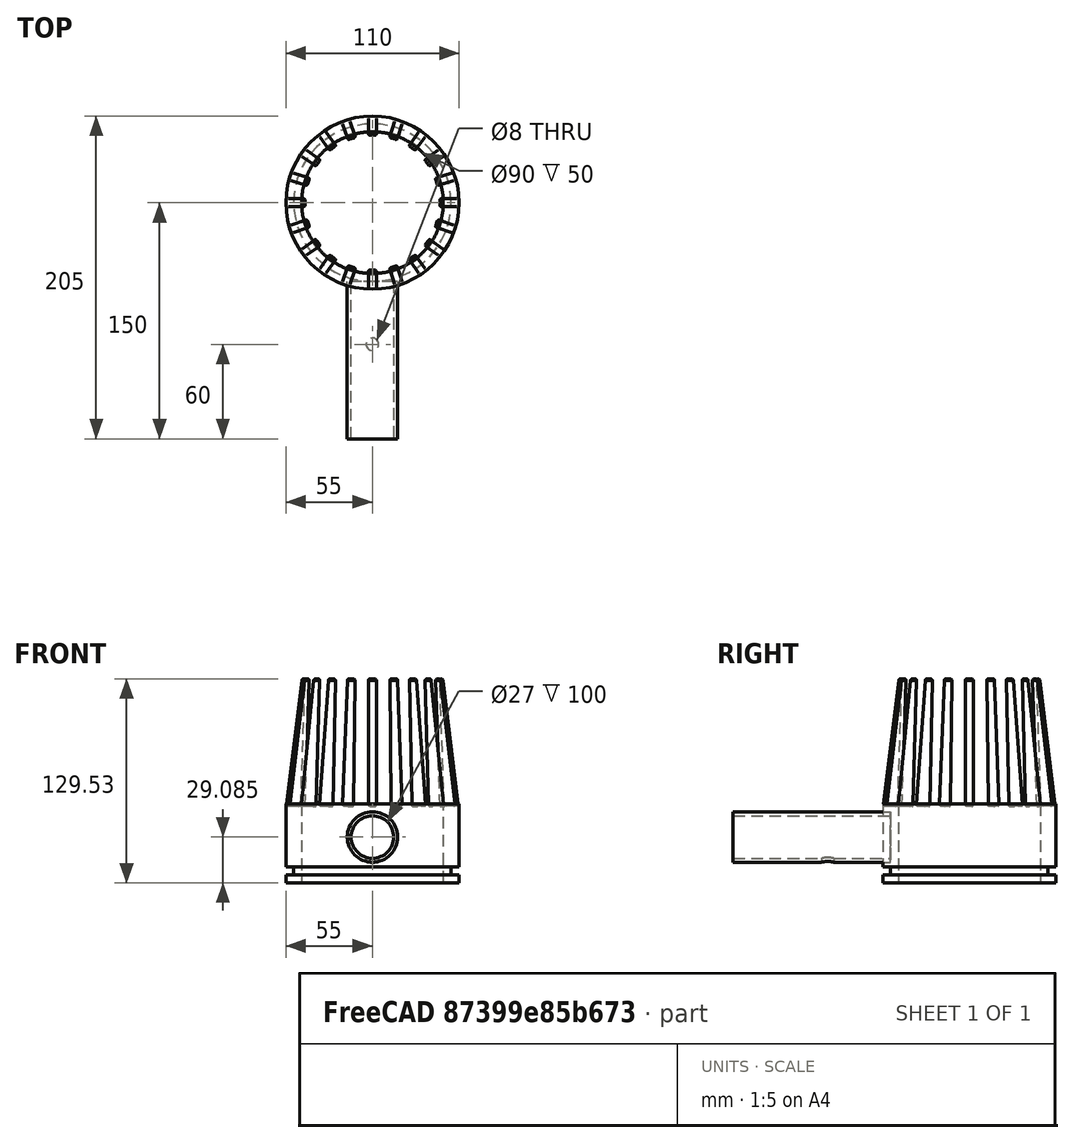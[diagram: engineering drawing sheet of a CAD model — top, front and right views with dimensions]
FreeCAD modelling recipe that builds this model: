
FCSTD DOCUMENT  (FreeCAD 1.1RUnknown)
Label: Picker
License: All rights reserved
LicenseURL: https://en.wikipedia.org/wiki/All_rights_reserved
objects: Part::Fillet×20, Sketcher::SketchObject×5, Part::Face×5, Part::Extrusion×5, Part::Cut×2, Part::Compound×2, Part::Plane×1
note: 45 computed .brp shape members not serialized (recipe doc carries the construction recipe); baked Part::Feature solids carry a one-line shape summary decoded from their .brp

FEATURE [Sketcher::SketchObject] Sketch
  ArcFitTolerance = 1e-06
  ExternalTypes = [0]
  FullyConstrained = true
  MakeInternals = false
  _ExternalGeoVersion = 1
  sketch-geometry (2):
    g0: Circle CenterX=0 CenterY=0 CenterZ=0 NormalX=0 NormalY=0 NormalZ=1 AngleXU=0 Radius=45
    g1: Circle CenterX=0 CenterY=0 CenterZ=0 NormalX=0 NormalY=0 NormalZ=1 AngleXU=0 Radius=55
  constraints (4):
    c: Diameter(g0) = 90
    c: Coincident(g0,g-1)
    c: Diameter(g1) = 110
    c: Coincident(g1,g0)
FEATURE [Part::Face] Face
  FaceMakerClass = Part::FaceMakerBullseye
  Sources = -> [Sketch]
FEATURE [Part::Extrusion] Extrude
  Base = -> Sketch
  Dir = (0,0,1)
  DirMode = 2
  FaceMakerClass = Part::FaceMakerBullseye
  FaceMakerMode = 3
  InnerWireTaper = 0
  LengthFwd = 40
  LengthRev = 10
  Solid = true
  Symmetric = false
FEATURE [Sketcher::SketchObject] Sketch001
  ArcFitTolerance = 1e-06
  AttachmentSupport = -> [Face]
  ExternalTypes = [0]
  FullyConstrained = true
  MakeInternals = false
  MapMode = 2
  _ExternalGeoVersion = 1
  sketch-geometry (2):
    g0: Circle CenterX=0 CenterY=0 CenterZ=0 NormalX=0 NormalY=0 NormalZ=1 AngleXU=0 Radius=55
    g1: Circle CenterX=0 CenterY=0 CenterZ=0 NormalX=0 NormalY=0 NormalZ=1 AngleXU=0 Radius=50
  constraints (4):
    c: Diameter(g0) = 110
    c: Coincident(g0,g-1)
    c: Diameter(g1) = 100
    c: Coincident(g1,g0)
FEATURE [Part::Face] Face001
  FaceMakerClass = Part::FaceMakerBullseye
  Sources = -> [Sketch001]
FEATURE [Part::Extrusion] Extrude001
  Base = -> Face001
  Dir = (0,0,1)
  DirMode = 2
  FaceMakerClass = Part::FaceMakerBullseye
  FaceMakerMode = 3
  InnerWireTaper = 0
  LengthFwd = 0
  LengthRev = 5
  Solid = false
  Symmetric = false
FEATURE [Part::Cut] Cut
  Base = -> Extrude
  Refine = true
  Tool = -> Extrude001
FEATURE [Sketcher::SketchObject] Sketch002
  ArcFitTolerance = 1e-06
  ExternalTypes = [0]
  FullyConstrained = true
  MakeInternals = false
  Placement = pos=(0,0,0) rot=(1,0,0;1.5708rad)
  _ExternalGeoVersion = 1
  sketch-geometry (6):
    g0: LineSegment StartX=-54 StartY=40 StartZ=0 EndX=-45 EndY=40 EndZ=0
    g1: LineSegment StartX=-45 StartY=40 StartZ=0 EndX=-45 EndY=120 EndZ=0
    g2: ArcOfCircle CenterX=-46 CenterY=120 CenterZ=0 NormalX=0 NormalY=0 NormalZ=1 AngleXU=0 Radius=1 StartAngle=-1.8e-15 EndAngle=1.5708
    g3: LineSegment StartX=-54 StartY=40 StartZ=0 EndX=-47 EndY=120 EndZ=0
    g4: ArcOfCircle CenterX=-46 CenterY=120 CenterZ=0 NormalX=0 NormalY=0 NormalZ=1 AngleXU=0 Radius=1 StartAngle=1.5708 EndAngle=3.14159
    g5: LineSegment [constr] StartX=-54 StartY=40 StartZ=0 EndX=0 EndY=40 EndZ=0
  constraints (19):
    c: Horizontal(g0)
    c: Distance(g1) = 80
    c: Vertical(g1)
    c: Coincident(g1,g0)
    c: Angle(g2) = 1.5708
    c: Coincident(g2,g1)
    c: Horizontal(g2,g1)
    c: Radius(g2) = 1
    c: Coincident(g3,g0)
    c: Coincident(g4,g2)
    c: Coincident(g4,g2)
    c: Coincident(g4,g3)
    c: Horizontal(g3,g2)
    c: Coincident(g5,g0)
    c: PointOnObject(g5,g-2)
    c: Horizontal(g5)
    c: Distance(g5,g-1) = 40
    c: DistanceX(g-2,g0) = -45
    c: Distance(g0) = 9
FEATURE [Part::Face] Face002
  FaceMakerClass = Part::FaceMakerBullseye
  Sources = -> [Sketch002]
FEATURE [Part::Extrusion] Extrude002
  Base = -> Sketch002
  Dir = (0,-1,2e-16)
  DirMode = 2
  FaceMakerClass = Part::FaceMakerBullseye
  FaceMakerMode = 3
  InnerWireTaper = 0
  LengthFwd = 5
  LengthRev = 5
  Placement = pos=(-2,0,0) rot=(0,1,0;0.034907rad)
  Solid = true
  Symmetric = true
FEATURE [Part::Fillet] Fillet  label="Bristle"
  Base = -> Extrude002
  EdgeLinks = -> Extrude002 [Edge3,Edge4,Edge6,Edge7,Edge9,Edge10,Edge12,Edge13,Edge14,Edge15]
  Edges = 10 edges r=1: [Edge3,Edge4,Edge6,Edge7,Edge9,Edge10,Edge12,Edge13,Edge14,Edge15]
FEATURE [Part::Fillet] Fillet001  label="Bristle001"
  Base = -> Extrude002
  EdgeLinks = -> Extrude002 [Edge3,Edge4,Edge6,Edge7,Edge9,Edge10,Edge12,Edge13,Edge14,Edge15]
  Edges = 10 edges r=1: [Edge3,Edge4,Edge6,Edge7,Edge9,Edge10,Edge12,Edge13,Edge14,Edge15]
  Placement = pos=(0,0,0) rot=(0,0,1;0.314159rad)
FEATURE [Part::Fillet] Fillet002  label="Bristle002"
  Base = -> Extrude002
  EdgeLinks = -> Extrude002 [Edge3,Edge4,Edge6,Edge7,Edge9,Edge10,Edge12,Edge13,Edge14,Edge15]
  Edges = 10 edges r=1: [Edge3,Edge4,Edge6,Edge7,Edge9,Edge10,Edge12,Edge13,Edge14,Edge15]
  Placement = pos=(0,0,0) rot=(0,0,1;0.628319rad)
FEATURE [Part::Fillet] Fillet003  label="Bristle003"
  Base = -> Extrude002
  EdgeLinks = -> Extrude002 [Edge3,Edge4,Edge6,Edge7,Edge9,Edge10,Edge12,Edge13,Edge14,Edge15]
  Edges = 10 edges r=1: [Edge3,Edge4,Edge6,Edge7,Edge9,Edge10,Edge12,Edge13,Edge14,Edge15]
  Placement = pos=(0,0,0) rot=(0,0,1;0.942478rad)
FEATURE [Part::Fillet] Fillet004  label="Bristle004"
  Base = -> Extrude002
  EdgeLinks = -> Extrude002 [Edge3,Edge4,Edge6,Edge7,Edge9,Edge10,Edge12,Edge13,Edge14,Edge15]
  Edges = 10 edges r=1: [Edge3,Edge4,Edge6,Edge7,Edge9,Edge10,Edge12,Edge13,Edge14,Edge15]
  Placement = pos=(0,0,0) rot=(0,0,1;1.25664rad)
FEATURE [Part::Fillet] Fillet005  label="Bristle005"
  Base = -> Extrude002
  EdgeLinks = -> Extrude002 [Edge3,Edge4,Edge6,Edge7,Edge9,Edge10,Edge12,Edge13,Edge14,Edge15]
  Edges = 10 edges r=1: [Edge3,Edge4,Edge6,Edge7,Edge9,Edge10,Edge12,Edge13,Edge14,Edge15]
  Placement = pos=(0,0,0) rot=(0,0,1;1.5708rad)
FEATURE [Part::Fillet] Fillet006  label="Bristle006"
  Base = -> Extrude002
  EdgeLinks = -> Extrude002 [Edge3,Edge4,Edge6,Edge7,Edge9,Edge10,Edge12,Edge13,Edge14,Edge15]
  Edges = 10 edges r=1: [Edge3,Edge4,Edge6,Edge7,Edge9,Edge10,Edge12,Edge13,Edge14,Edge15]
  Placement = pos=(0,0,0) rot=(0,0,1;1.88496rad)
FEATURE [Part::Fillet] Fillet007  label="Bristle007"
  Base = -> Extrude002
  EdgeLinks = -> Extrude002 [Edge3,Edge4,Edge6,Edge7,Edge9,Edge10,Edge12,Edge13,Edge14,Edge15]
  Edges = 10 edges r=1: [Edge3,Edge4,Edge6,Edge7,Edge9,Edge10,Edge12,Edge13,Edge14,Edge15]
  Placement = pos=(0,0,0) rot=(0,0,1;2.19911rad)
FEATURE [Part::Fillet] Fillet008  label="Bristle008"
  Base = -> Extrude002
  EdgeLinks = -> Extrude002 [Edge3,Edge4,Edge6,Edge7,Edge9,Edge10,Edge12,Edge13,Edge14,Edge15]
  Edges = 10 edges r=1: [Edge3,Edge4,Edge6,Edge7,Edge9,Edge10,Edge12,Edge13,Edge14,Edge15]
  Placement = pos=(0,0,0) rot=(0,0,1;2.51327rad)
FEATURE [Part::Fillet] Fillet009  label="Bristle009"
  Base = -> Extrude002
  EdgeLinks = -> Extrude002 [Edge3,Edge4,Edge6,Edge7,Edge9,Edge10,Edge12,Edge13,Edge14,Edge15]
  Edges = 10 edges r=1: [Edge3,Edge4,Edge6,Edge7,Edge9,Edge10,Edge12,Edge13,Edge14,Edge15]
  Placement = pos=(0,0,0) rot=(0,0,1;2.82743rad)
FEATURE [Part::Fillet] Fillet010  label="Bristle010"
  Base = -> Extrude002
  EdgeLinks = -> Extrude002 [Edge3,Edge4,Edge6,Edge7,Edge9,Edge10,Edge12,Edge13,Edge14,Edge15]
  Edges = 10 edges r=1: [Edge3,Edge4,Edge6,Edge7,Edge9,Edge10,Edge12,Edge13,Edge14,Edge15]
  Placement = pos=(0,0,0) rot=(0,0,1;3.14159rad)
FEATURE [Part::Fillet] Fillet011  label="Bristle011"
  Base = -> Extrude002
  EdgeLinks = -> Extrude002 [Edge3,Edge4,Edge6,Edge7,Edge9,Edge10,Edge12,Edge13,Edge14,Edge15]
  Edges = 10 edges r=1: [Edge3,Edge4,Edge6,Edge7,Edge9,Edge10,Edge12,Edge13,Edge14,Edge15]
  Placement = pos=(0,0,0) rot=(0,0,1;3.45575rad)
FEATURE [Part::Fillet] Fillet012  label="Bristle012"
  Base = -> Extrude002
  EdgeLinks = -> Extrude002 [Edge3,Edge4,Edge6,Edge7,Edge9,Edge10,Edge12,Edge13,Edge14,Edge15]
  Edges = 10 edges r=1: [Edge3,Edge4,Edge6,Edge7,Edge9,Edge10,Edge12,Edge13,Edge14,Edge15]
  Placement = pos=(0,0,0) rot=(0,0,1;3.76991rad)
FEATURE [Part::Fillet] Fillet013  label="Bristle013"
  Base = -> Extrude002
  EdgeLinks = -> Extrude002 [Edge3,Edge4,Edge6,Edge7,Edge9,Edge10,Edge12,Edge13,Edge14,Edge15]
  Edges = 10 edges r=1: [Edge3,Edge4,Edge6,Edge7,Edge9,Edge10,Edge12,Edge13,Edge14,Edge15]
  Placement = pos=(0,0,0) rot=(0,0,1;4.08407rad)
FEATURE [Part::Fillet] Fillet014  label="Bristle014"
  Base = -> Extrude002
  EdgeLinks = -> Extrude002 [Edge3,Edge4,Edge6,Edge7,Edge9,Edge10,Edge12,Edge13,Edge14,Edge15]
  Edges = 10 edges r=1: [Edge3,Edge4,Edge6,Edge7,Edge9,Edge10,Edge12,Edge13,Edge14,Edge15]
  Placement = pos=(0,0,0) rot=(0,0,1;4.39823rad)
FEATURE [Part::Fillet] Fillet015  label="Bristle015"
  Base = -> Extrude002
  EdgeLinks = -> Extrude002 [Edge3,Edge4,Edge6,Edge7,Edge9,Edge10,Edge12,Edge13,Edge14,Edge15]
  Edges = 10 edges r=1: [Edge3,Edge4,Edge6,Edge7,Edge9,Edge10,Edge12,Edge13,Edge14,Edge15]
  Placement = pos=(0,0,0) rot=(0,0,1;4.71239rad)
FEATURE [Part::Fillet] Fillet016  label="Bristle016"
  Base = -> Extrude002
  EdgeLinks = -> Extrude002 [Edge3,Edge4,Edge6,Edge7,Edge9,Edge10,Edge12,Edge13,Edge14,Edge15]
  Edges = 10 edges r=1: [Edge3,Edge4,Edge6,Edge7,Edge9,Edge10,Edge12,Edge13,Edge14,Edge15]
  Placement = pos=(0,0,0) rot=(0,0,1;5.02655rad)
FEATURE [Part::Fillet] Fillet017  label="Bristle017"
  Base = -> Extrude002
  EdgeLinks = -> Extrude002 [Edge3,Edge4,Edge6,Edge7,Edge9,Edge10,Edge12,Edge13,Edge14,Edge15]
  Edges = 10 edges r=1: [Edge3,Edge4,Edge6,Edge7,Edge9,Edge10,Edge12,Edge13,Edge14,Edge15]
  Placement = pos=(0,0,0) rot=(0,0,1;5.34071rad)
FEATURE [Part::Fillet] Fillet018  label="Bristle018"
  Base = -> Extrude002
  EdgeLinks = -> Extrude002 [Edge3,Edge4,Edge6,Edge7,Edge9,Edge10,Edge12,Edge13,Edge14,Edge15]
  Edges = 10 edges r=1: [Edge3,Edge4,Edge6,Edge7,Edge9,Edge10,Edge12,Edge13,Edge14,Edge15]
  Placement = pos=(0,0,0) rot=(0,0,1;5.65487rad)
FEATURE [Part::Fillet] Fillet019  label="Bristle019"
  Base = -> Extrude002
  EdgeLinks = -> Extrude002 [Edge3,Edge4,Edge6,Edge7,Edge9,Edge10,Edge12,Edge13,Edge14,Edge15]
  Edges = 10 edges r=1: [Edge3,Edge4,Edge6,Edge7,Edge9,Edge10,Edge12,Edge13,Edge14,Edge15]
  Placement = pos=(0,0,0) rot=(0,0,1;5.96903rad)
FEATURE [Part::Compound] Compound  label="Comb"
  Links = -> [Fillet019,Fillet,Fillet001,Fillet002,Fillet003,Fillet004,Fillet005,Fillet006,Fillet007,Fillet008,Fillet009,Fillet010,Fillet011,Fillet012,Fillet013,Fillet014,Fillet015,Fillet016,Fillet017,Fillet018]
  Placement = pos=(0,0,-3) rot=(0,0,1;0rad)
FEATURE [Sketcher::SketchObject] Sketch003
  ArcFitTolerance = 1e-06
  ExternalTypes = [0]
  FullyConstrained = false
  MakeInternals = false
  Placement = pos=(0,0,0) rot=(1,0,0;1.5708rad)
  _ExternalGeoVersion = 1
  sketch-geometry (2):
    g0: Circle CenterX=0 CenterY=134.085 CenterZ=0 NormalX=0 NormalY=0 NormalZ=1 AngleXU=0 Radius=13.5
    g1: Circle CenterX=0 CenterY=134.085 CenterZ=0 NormalX=0 NormalY=0 NormalZ=1 AngleXU=0 Radius=16
  constraints (4):
    c: Diameter(g0) = 27
    c: PointOnObject(g0,g-2)
    c: Diameter(g1) = 32
    c: Coincident(g1,g0)
FEATURE [Part::Face] Face003
  FaceMakerClass = Part::FaceMakerBullseye
  Sources = -> [Sketch003]
FEATURE [Part::Extrusion] Extrude003
  Base = -> Sketch003
  Dir = (0,-1,2e-16)
  DirMode = 2
  FaceMakerClass = Part::FaceMakerBullseye
  FaceMakerMode = 3
  InnerWireTaper = 0
  LengthFwd = 100
  LengthRev = 0
  Placement = pos=(0,-50,-115) rot=(0,0,1;0rad)
  Solid = true
  Symmetric = false
FEATURE [Sketcher::SketchObject] Sketch004
  ArcFitTolerance = 1e-06
  ExternalTypes = [0]
  FullyConstrained = false
  MakeInternals = false
  _ExternalGeoVersion = 1
  sketch-geometry (2):
    g0: Circle CenterX=0 CenterY=-90 CenterZ=0 NormalX=0 NormalY=0 NormalZ=1 AngleXU=0 Radius=4
    g1: GeomPoint [constr] X=0 Y=-150 Z=0
  constraints (4):
    c: Diameter(g0) = 8
    c: PointOnObject(g0,g-2)
    c: PointOnObject(g1,g-2)
    c: Distance(g0,g1) = 60
FEATURE [Part::Face] Face004
  FaceMakerClass = Part::FaceMakerBullseye
  Sources = -> [Sketch004]
FEATURE [Part::Extrusion] Extrude004
  Base = -> Face004
  Dir = (0,0,1)
  DirMode = 2
  FaceMakerClass = Part::FaceMakerBullseye
  FaceMakerMode = 3
  InnerWireTaper = 0
  LengthFwd = 10
  LengthRev = 0
  Solid = false
  Symmetric = false
FEATURE [Part::Cut] Cut001
  Base = -> Extrude003
  Refine = true
  Tool = -> Extrude004
FEATURE [Part::Compound] Compound001  label="Picker"
  Links = -> [Compound,Cut001,Cut]
FEATURE [Part::Plane] Plane
  AttacherType = Attacher::AttachEngine3D
  Length = 10
  Width = 10
